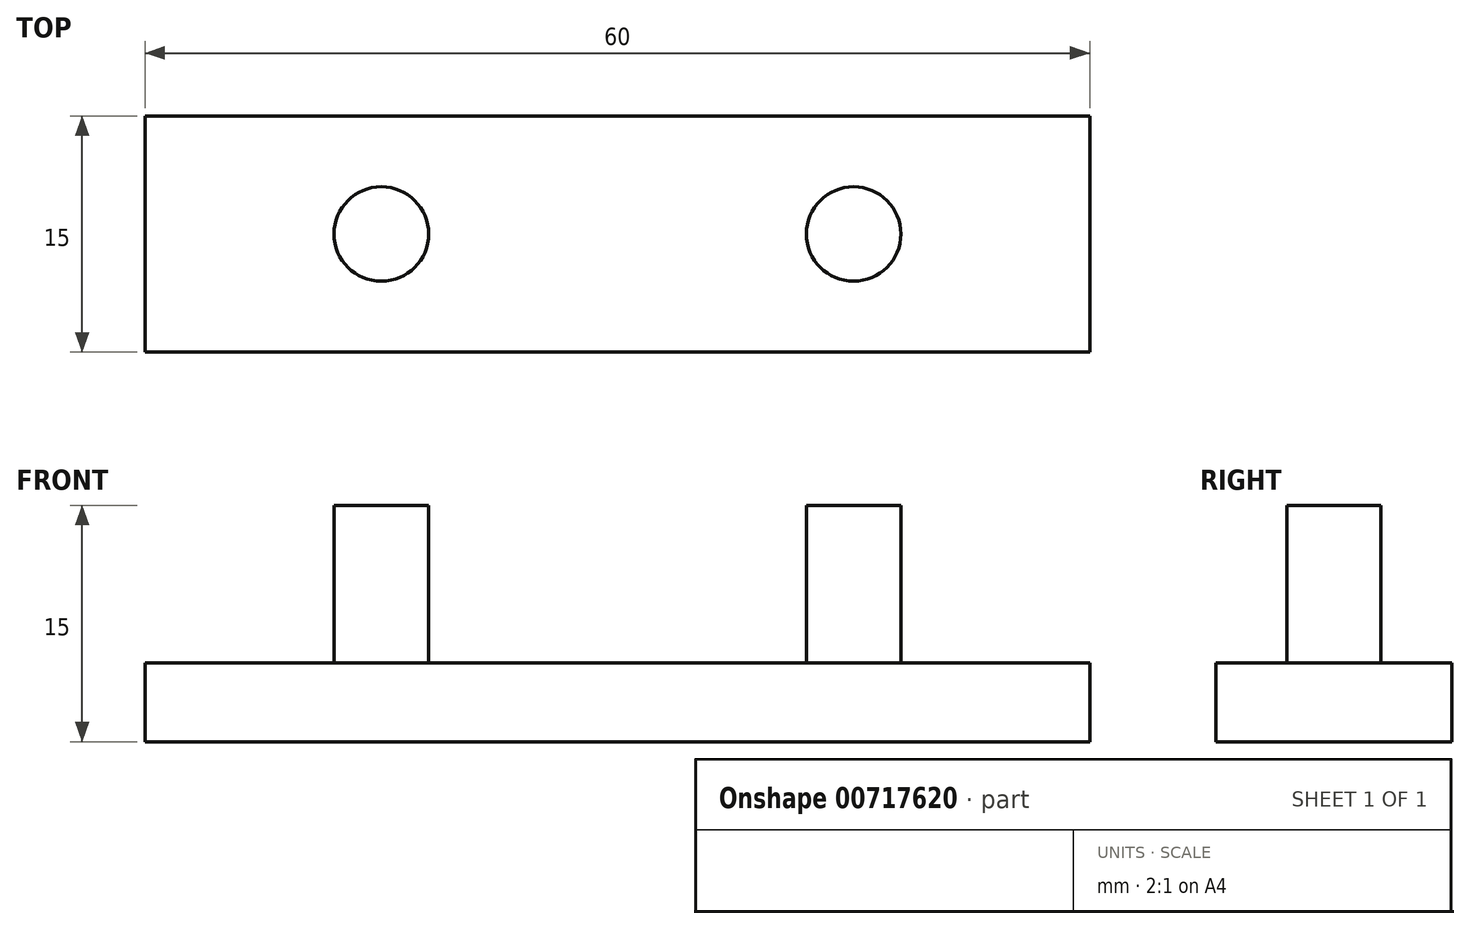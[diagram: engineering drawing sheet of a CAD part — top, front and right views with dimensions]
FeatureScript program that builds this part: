
annotation { "Feature Type Name" : "Feature", "Feature Type Description" : "" }
export const myFeature = defineFeature(function(context is Context, id is Id, definition is map)
    precondition{}
    {
        {
            var Q0;
            Q0=qCreatedBy(makeId("Top.planeOp"),FACE);
            var sketch = newSketch(context, id + "F0", { "sketchPlane" : qUnion([Q0])});
            skLineSegment(sketch, "E0.bottom", {"start": v(-30, -7.5) * mm, "end": v(30, -7.5) * mm});
            skLineSegment(sketch, "E0.top", {"start": v(-30, 7.5) * mm, "end": v(30, 7.5) * mm});
            skLineSegment(sketch, "E0.left", {"start": v(-30, -7.5) * mm, "end": v(-30, 7.5) * mm});
            skLineSegment(sketch, "E0.right", {"start": v(30, -7.5) * mm, "end": v(30, 7.5) * mm});
            skPoint(sketch, "E0.middle", {"position": v(0, 0) * mm});
            skSolve(sketch);
        }
        {
            var Q0;
            Q0=makeQuery(id+"F0.imprint","IMPRINT",FACE,{"disambiguationData":[TD([[makeQuery(id+"F0.imprint","IMPRINT",EDGE,{"derivedFrom":sQuery(id+"F0.wireOp",EDGE,"E0.bottom")}),1.0]])]});
            extrude(context, id + "F1", {"entities" : qUnion([Q0]), "depth" : 5 * mm, "offsetDistance" : 25 * mm});
        }
        {
            var Q0;
            Q0=makeQuery(id+"F1.opExtrude","CAP_FACE",FACE,{"disambiguationData":[OSD([sQuery(id+"F0.wireOp",EDGE,"E0.bottom"),sQuery(id+"F0.wireOp",EDGE,"E0.top"),sQuery(id+"F0.wireOp",EDGE,"E0.left"),sQuery(id+"F0.wireOp",EDGE,"E0.right")])],"isStart":false});
            var sketch = newSketch(context, id + "F2", { "sketchPlane" : qUnion([Q0])});
            skPoint(sketch, "E1", {"position": v(-15, 0) * mm});
            skPoint(sketch, "E2", {"position": v(15, 0) * mm});
            skCircle(sketch, "E3", {"center": v(-15, 0) * mm, "radius": 3 * mm});
            skCircle(sketch, "E4", {"center": v(15, 0) * mm, "radius": 3 * mm});
            skSolve(sketch);
        }
        {
            var Q0;
            Q0=makeQuery(id+"F2.imprint","IMPRINT",FACE,{"disambiguationData":[TD([[makeQuery(id+"F2.imprint","IMPRINT",EDGE,{"derivedFrom":sQuery(id+"F2.wireOp",EDGE,"E3")}),1.0]])]});
            var Q1;
            Q1=makeQuery(id+"F2.imprint","IMPRINT",FACE,{"disambiguationData":[TD([[makeQuery(id+"F2.imprint","IMPRINT",EDGE,{"derivedFrom":sQuery(id+"F2.wireOp",EDGE,"E4")}),1.0]])]});
            extrude(context, id + "F3", {"entities" : qUnion([Q0, Q1]), "operationType" : NewBodyOperationType.ADD, "depth" : 10 * mm, "offsetDistance" : 25 * mm});
        }
    });
